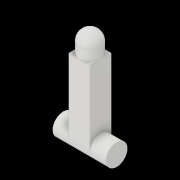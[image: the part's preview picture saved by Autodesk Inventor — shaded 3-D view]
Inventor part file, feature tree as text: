
AUTODESK INVENTOR PART (.ipt)
format: ipt  version: 2019 (Build 230136000, 136)  size: 110,080 bytes
history: native  units: mm
features: sketch x4, extrude x3, revolve x1, projected_geometry x1
ambient origin geometry x8: Origin, YZ Plane, XZ Plane, XY Plane, X Axis, Y Axis, Z Axis, Center Point
bodies: Body1 (feature_tree)
feature tree (9):
  extrude  "돌출4"  Depth=20.0mm
  extrude  "돌출5"  Depth=50.0mm TaperAngle=0.0deg
  extrude  "돌출6"  Depth=20.0mm
  revolve  "회전2"
  sketch  "스케치5"
  sketch  "스케치6"
  sketch  "스케치7"
  sketch  "스케치8"
  projected_geometry  "투영된 루프2"
